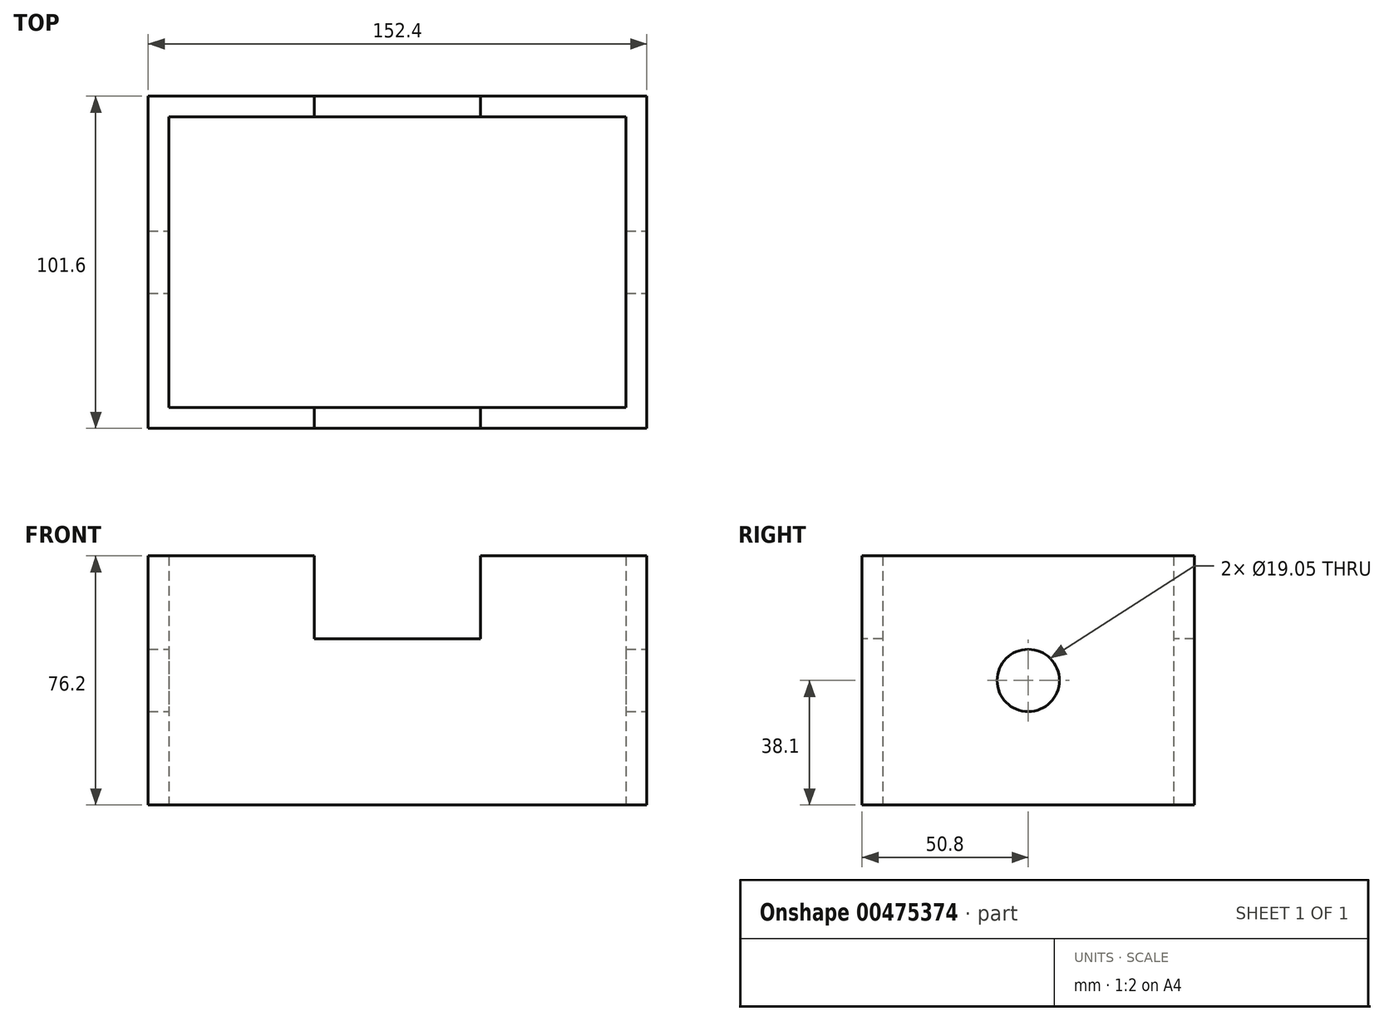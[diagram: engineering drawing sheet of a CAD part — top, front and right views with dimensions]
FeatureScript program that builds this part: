
annotation { "Feature Type Name" : "Feature", "Feature Type Description" : "" }
export const myFeature = defineFeature(function(context is Context, id is Id, definition is map)
    precondition{}
    {
        {
            var Q0;
            Q0=qCreatedBy(makeId("Top.planeOp"),FACE);
            var sketch = newSketch(context, id + "F0", { "sketchPlane" : qUnion([Q0])});
            skLineSegment(sketch, "E0.bottom", {"start": v(76.2, -50.8) * mm, "end": v(-76.2, -50.8) * mm});
            skLineSegment(sketch, "E0.top", {"start": v(76.2, 50.8) * mm, "end": v(-76.2, 50.8) * mm});
            skLineSegment(sketch, "E0.left", {"start": v(76.2, -50.8) * mm, "end": v(76.2, 50.8) * mm});
            skLineSegment(sketch, "E0.right", {"start": v(-76.2, -50.8) * mm, "end": v(-76.2, 50.8) * mm});
            skPoint(sketch, "E0.middle", {"position": v(0, 0) * mm});
            skLineSegment(sketch, "E1.bottom", {"start": v(69.85, -44.45) * mm, "end": v(-69.85, -44.45) * mm});
            skLineSegment(sketch, "E1.top", {"start": v(69.85, 44.45) * mm, "end": v(-69.85, 44.45) * mm});
            skLineSegment(sketch, "E1.left", {"start": v(69.85, -44.45) * mm, "end": v(69.85, 44.45) * mm});
            skLineSegment(sketch, "E1.right", {"start": v(-69.85, -44.45) * mm, "end": v(-69.85, 44.45) * mm});
            skSolve(sketch);
        }
        {
            var Q0;
            Q0=makeQuery(id+"F0.imprint","IMPRINT",FACE,{"disambiguationData":[TD([[makeQuery(id+"F0.imprint","IMPRINT",EDGE,{"derivedFrom":sQuery(id+"F0.wireOp",EDGE,"E0.bottom")}),-1.0]])]});
            extrude(context, id + "F1", {"entities" : qUnion([Q0]), "depth" : 76.2 * mm});
        }
        {
            var Q0;
            Q0=makeQuery(id+"F1.opExtrude","SWEPT_FACE",FACE,{"disambiguationData":[OSD([sQuery(id+"F0.wireOp",EDGE,"E0.bottom")])]});
            var sketch = newSketch(context, id + "F2", { "sketchPlane" : qUnion([Q0])});
            skLineSegment(sketch, "E2.bottom", {"start": v(-25.4, 76.2) * mm, "end": v(25.4, 76.2) * mm});
            skLineSegment(sketch, "E2.top", {"start": v(-25.4, 50.8) * mm, "end": v(25.4, 50.8) * mm});
            skLineSegment(sketch, "E2.left", {"start": v(-25.4, 76.2) * mm, "end": v(-25.4, 50.8) * mm});
            skLineSegment(sketch, "E2.right", {"start": v(25.4, 76.2) * mm, "end": v(25.4, 50.8) * mm});
            skSolve(sketch);
        }
        {
            var Q0;
            Q0 = qSketchRegion(id + "F2", true);
            var Q1;
            Q1=makeQuery(id+"F2.imprint","IMPRINT",FACE,{"disambiguationData":[TD([[makeQuery(id+"F2.imprint","IMPRINT",EDGE,{"derivedFrom":sQuery(id+"F2.wireOp",EDGE,"E2.bottom")}),1.0]])]});
            extrude(context, id + "F3", {"entities" : qUnion([Q0, Q1]), "operationType" : NewBodyOperationType.REMOVE, "endBound" : BoundingType.THROUGH_ALL, "oppositeDirection" : true, "depth" : 25.4 * mm});
        }
        {
            var Q0;
            Q0=makeQuery(id+"F1.opExtrude","SWEPT_FACE",FACE,{"disambiguationData":[OSD([sQuery(id+"F0.wireOp",EDGE,"E0.left")])]});
            var sketch = newSketch(context, id + "F4", { "sketchPlane" : qUnion([Q0])});
            skLineSegment(sketch, "E3", {"start": v(-50.8, 38.1) * mm, "end": v(0, 38.1) * mm, "construction": true});
            skLineSegment(sketch, "E4", {"start": v(0, 38.1) * mm, "end": v(0, 76.2) * mm, "construction": true});
            skCircle(sketch, "E5", {"center": v(0, 38.1) * mm, "radius": 9.53 * mm});
            skSolve(sketch);
        }
        {
            var Q0;
            Q0=makeQuery(id+"F4.imprint","IMPRINT",FACE,{"disambiguationData":[TD([[makeQuery(id+"F4.imprint","IMPRINT",EDGE,{"derivedFrom":sQuery(id+"F4.wireOp",EDGE,"E5")}),1.0]])]});
            extrude(context, id + "F5", {"entities" : qUnion([Q0]), "operationType" : NewBodyOperationType.REMOVE, "endBound" : BoundingType.THROUGH_ALL, "oppositeDirection" : true, "depth" : 25.4 * mm});
        }
    });
